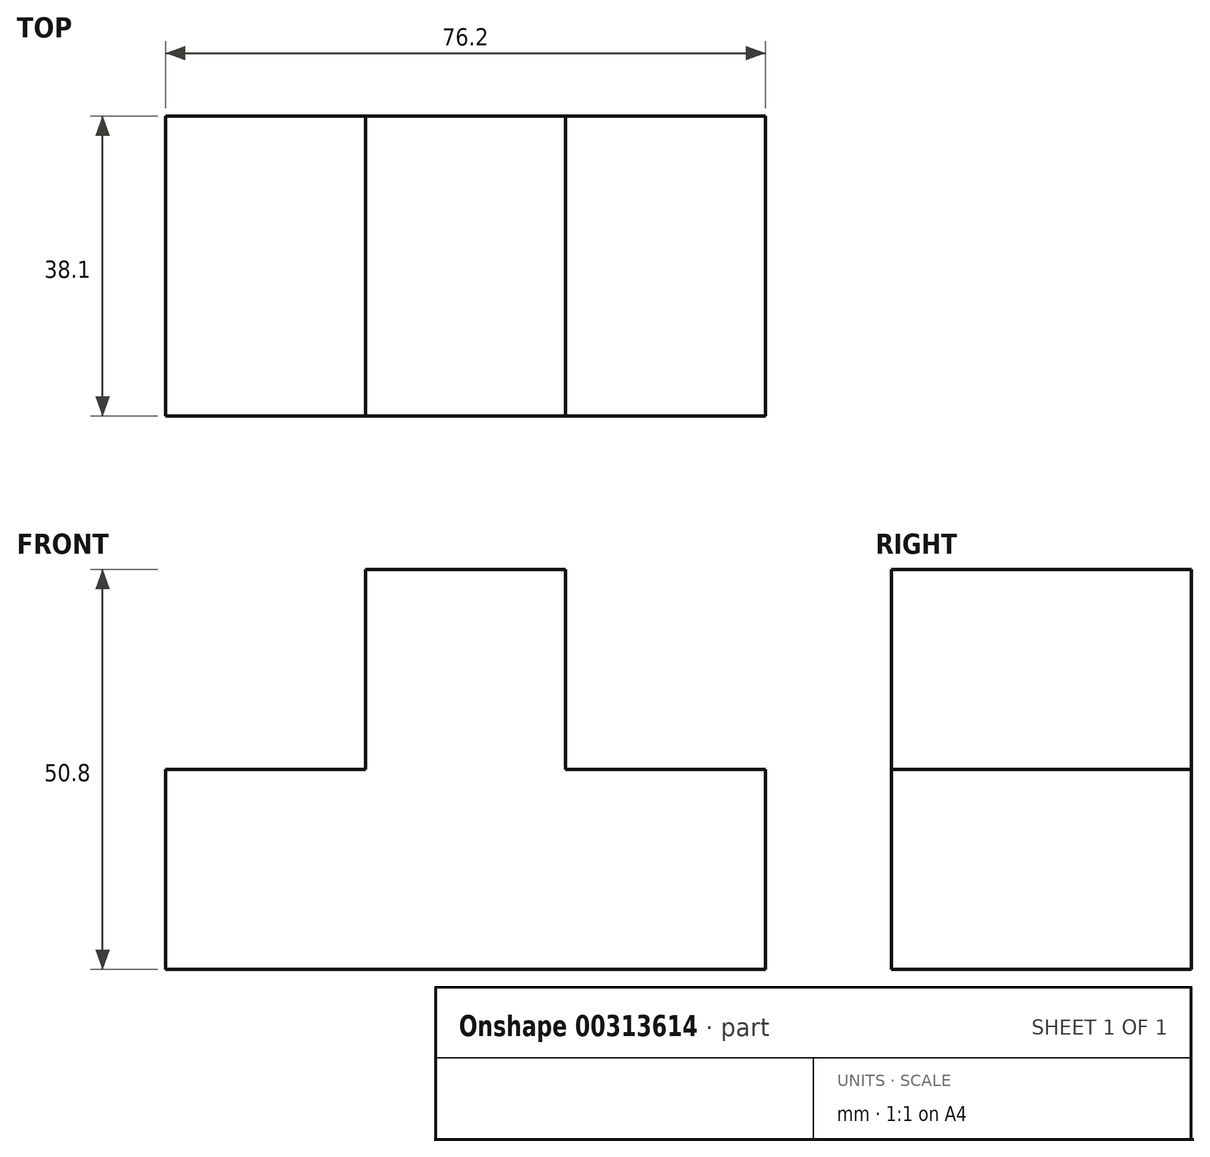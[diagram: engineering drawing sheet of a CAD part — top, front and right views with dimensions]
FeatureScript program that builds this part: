
annotation { "Feature Type Name" : "Feature", "Feature Type Description" : "" }
export const myFeature = defineFeature(function(context is Context, id is Id, definition is map)
    precondition{}
    {
        {
            var Q0;
            Q0=qCreatedBy(makeId("Front.planeOp"),FACE);
            var sketch = newSketch(context, id + "F0", { "sketchPlane" : qUnion([Q0])});
            skLineSegment(sketch, "E0", {"start": v(-40.27, -29.87) * mm, "end": v(35.93, -29.87) * mm});
            skLineSegment(sketch, "E1", {"start": v(35.93, -29.87) * mm, "end": v(35.93, -4.47) * mm});
            skLineSegment(sketch, "E2", {"start": v(35.93, -4.47) * mm, "end": v(10.53, -4.47) * mm});
            skLineSegment(sketch, "E3", {"start": v(10.53, -4.47) * mm, "end": v(10.53, 20.93) * mm});
            skLineSegment(sketch, "E4", {"start": v(10.53, 20.93) * mm, "end": v(-14.87, 20.93) * mm});
            skLineSegment(sketch, "E5", {"start": v(-14.87, 20.93) * mm, "end": v(-14.87, -4.47) * mm});
            skLineSegment(sketch, "E6", {"start": v(-14.87, -4.47) * mm, "end": v(-40.27, -4.47) * mm});
            skLineSegment(sketch, "E7", {"start": v(-40.27, -4.47) * mm, "end": v(-40.27, -29.87) * mm});
            skSolve(sketch);
        }
        {
            var Q0;
            Q0=makeQuery(id+"F0.imprint","IMPRINT",FACE,{"disambiguationData":[TD([[makeQuery(id+"F0.imprint","IMPRINT",EDGE,{"derivedFrom":sQuery(id+"F0.wireOp",EDGE,"E0")}),1.0]])]});
            extrude(context, id + "F1", {"entities" : qUnion([Q0]), "oppositeDirection" : true, "depth" : 38.1 * mm});
        }
    });
